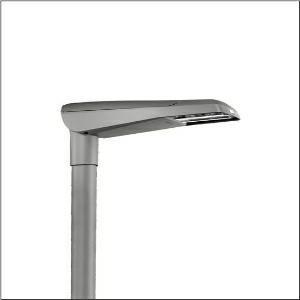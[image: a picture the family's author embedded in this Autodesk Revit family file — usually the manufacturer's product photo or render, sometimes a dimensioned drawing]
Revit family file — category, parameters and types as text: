
# Revit family: streetlight_sl_11_iq_micro___st1_2a_5xc1a61g08ce_6eb0
name_source: partatom
category: Lighting Fixtures
units: mm (PartAtom-declared; Revit-internal decimal feet)

## family parameters
Cut with Voids When Loaded = No
Host = Face
Light Source = No
Part Type = Normal
Room Calculation Point = No
Round Connector Dimension = Use Diameter
Shared = No

## types (1)
- --- (1 x LED, 1690 lm, 12.6 W, 2700K)
    Apparent Load = 13 VA
    CIE Flux Codes = 33 71 96 100 100
    Color Rendering = 70
    Color Temperature = 2700K
    Default Elevation = 1800 mm
    Description = Streetlight SL 11 iQ micro, mast luminaire, primary light control with 3 zone facetted reflector, of plastic, silver coated, highly specular, primary optical cover: cover, of PMMA, transparent, light distribution: ST1.2a, light emission: direct distribution, primary light characteristic: asymmetric, installation type: side-entry, post-top, lamps: LED, High Power LED, rated values: 1.690lm | 12,6W | 134,1lm/W (begin service life); end service life: 1.690lm | 12,9W; at 50% lumin. flux: 845lm | 6,8W | 124,3lm/W, colour temperature: 2700K, colour rendering: CRI > 70, light colour: 727, light setting 1 begin service life: 100% | 1.690lm | 12,6W | 134,1lm/W | 2.700K, light setting 1 end service life: 12,9W, further light settings possible, control: optimised constant luminous flux control (CLO 2.0), Desk-Remote (wireless, voltage-free reading and setting of iQ features in the workshop via application-optimized NFC function/RFID function), Light-Fading, Smart-Wire, Night-Set, Lumen-Switch, Temp-Guard, Auto-Match, Street-Remote, pre-setting: linear dimming characteristic, with cable H07RN-F 5x 1.5mm², mains connection: 230..240V, AC, 50/60Hz, connection cable pre-assembled, cable length: 5,5m, luminaire housing, of diecast aluminium, powder-coated, Siteco® metallic grey (DB 702S), please order mast flange separately, inclination adjustable without tools: 0°, 5°, 10°, 15° (post-top) | 0°, -5°, -10°, -15° (side-entry), sealing non-destructively replaceable, multi-level sealing system, length: 600mm, width: 174mm, height: 116mm, mast flange for spigot size: 42mm (side-entry): 5XC10008XM4, 60/48mm (side-entry/post-top): 5XC10108XM2, 76/60mm (side-entry/post-top): 5XC10108XM1, equipment: standard, protection rating (complete): IP66, insulation class (complete): insulation class II (safety insulation), certification: CE, ENEC, ENEC+, VDE, impact resistance: IK10, permissible operating ambient temperature for outdoor applications: -25..+50°C, standard-compliant lighting for roads and squares, Environmental Product Declaration (EPD) tested and certified by an independent institute, packaging unit: 1 piece

Light Distribution: ST1.2a
    Height = 116 mm
    Lamp = 1 x LED
    Lamp Light Flux = 1690 lm
    Lamp Power = 12.6 W
    Lamp count = 1
    Length = 600 mm
    Luminous efficacy = 134 lm/W
    Manufacturer = Siteco
    ModVariant = No
    Model = 5XC1A61G08CE
    Number of Poles = 1
    OnlyDefault = Yes
    Power Factor = 1
    Product Name = Streetlight SL 11 iQ micro | ST1.2a
    Product group = mast luminaire | pylon top
    ProductGroupID = 6100
    Protection Class = Protection class II
    Protection Degree = IP 66
    RLX_Detail_Level = 1
    RLX_Emergency_Light_Flux = 0 lm
    RLX_Emergency_Type = 0
    RLX_Emergency_Type_DB = No
    RlxData = <blob elided: 26565 chars, md5=13a42baf>
    Socket = socket
    Standby Power = 0 W
    System Light Flux = 1690 lm
    System Power = 13 W
    Type Comments = factory setting: luminous flux: 100 % | dim-lin: 254 | 229 mA
    Type Image = l_1006566.jpg
    URL = http://relux.com
    VarID = @adj_000823
    Voltage = 0 V
    Weight = 0.00 kg
    Width = 174 mm

## geometry (parser evidence)
native form markers: Blend x4, Sweep x11
no freeform markers — native parametric forms only
